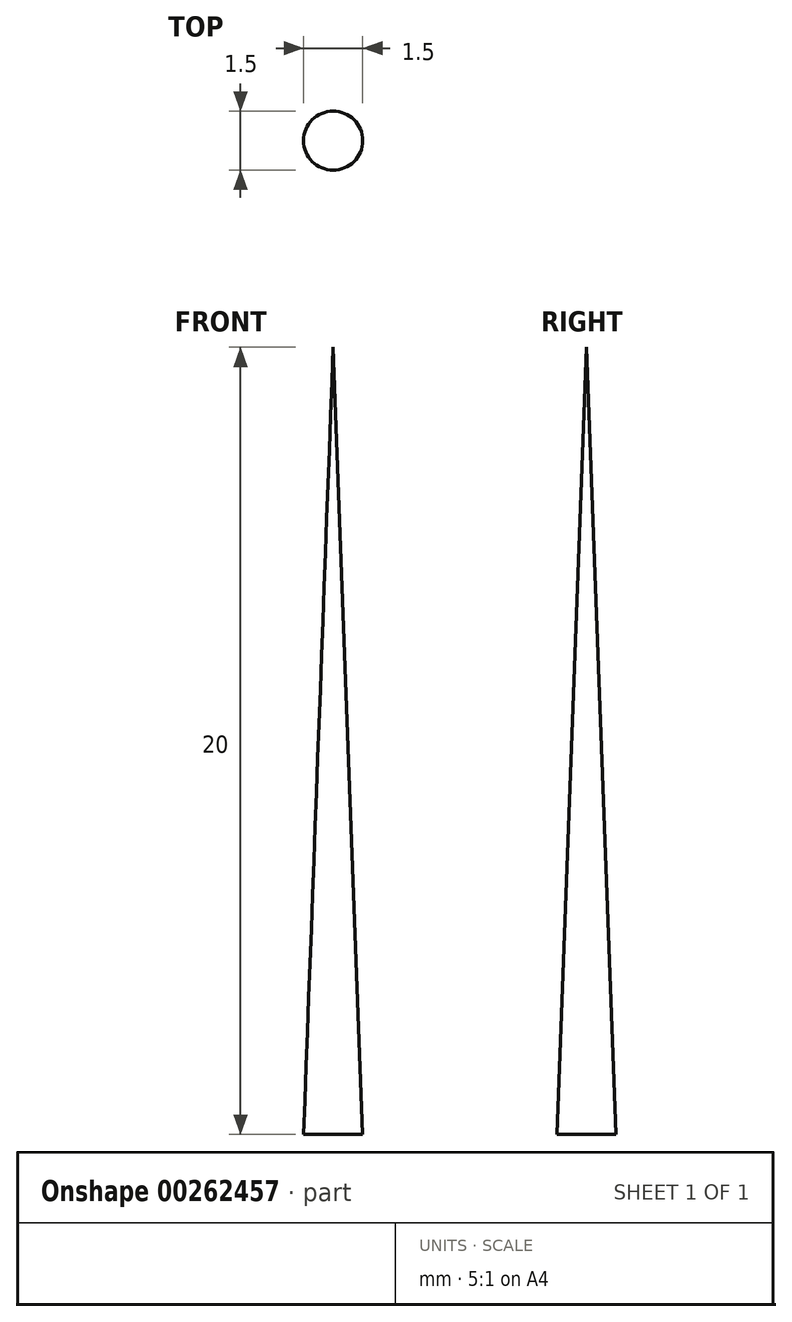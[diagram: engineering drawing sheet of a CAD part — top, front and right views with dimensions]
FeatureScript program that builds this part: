
annotation { "Feature Type Name" : "Feature", "Feature Type Description" : "" }
export const myFeature = defineFeature(function(context is Context, id is Id, definition is map)
    precondition{}
    {
        {
            var Q0;
            Q0=qCreatedBy(makeId("Front.planeOp"),FACE);
            var sketch = newSketch(context, id + "F0", { "sketchPlane" : qUnion([Q0])});
            skLineSegment(sketch, "E0", {"start": v(0, 0) * mm, "end": v(0, 20) * mm});
            skLineSegment(sketch, "E1", {"start": v(0, 0) * mm, "end": v(0.75, 0) * mm});
            skLineSegment(sketch, "E2", {"start": v(0, 20) * mm, "end": v(0.75, 0) * mm});
            skSolve(sketch);
        }
        {
            var Q0;
            Q0=makeQuery(id+"F0.imprint","IMPRINT",FACE,{"disambiguationData":[TD([[makeQuery(id+"F0.imprint","IMPRINT",EDGE,{"derivedFrom":sQuery(id+"F0.wireOp",EDGE,"E0")}),-1.0]])]});
            var Q1;
            Q1=sQuery(id+"F0.wireOp",EDGE,"E0");
            revolve(context, id + "F1", {"entities" : qUnion([Q0]), "axis" : qUnion([Q1]), "revolveType" : RevolveType.FULL});
        }
    });
